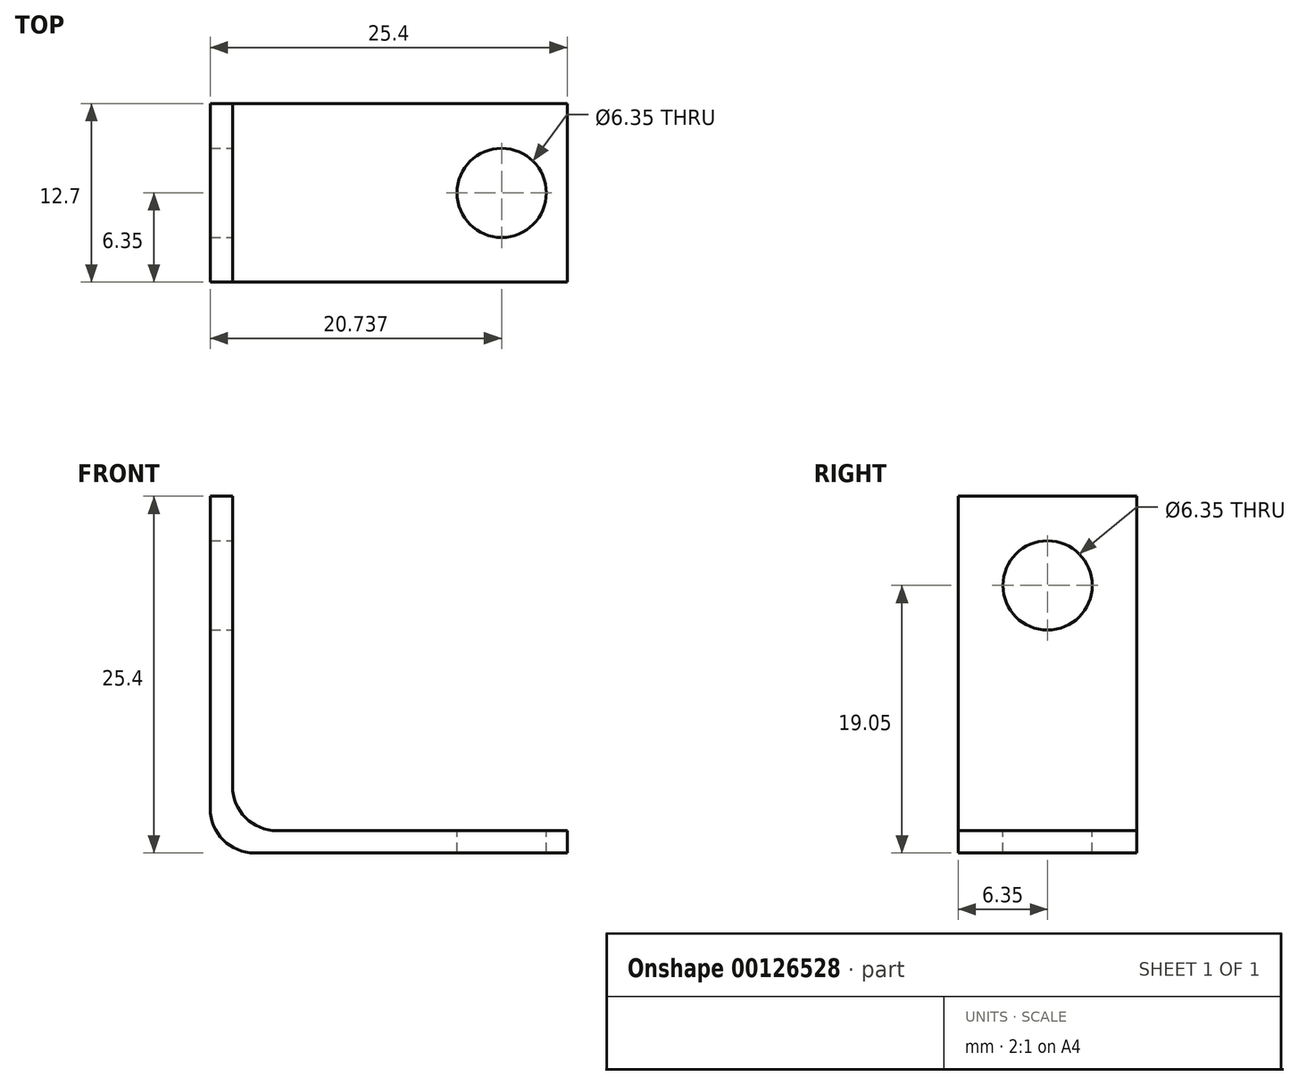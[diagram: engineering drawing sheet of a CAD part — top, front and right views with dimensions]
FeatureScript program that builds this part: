
annotation { "Feature Type Name" : "Feature", "Feature Type Description" : "" }
export const myFeature = defineFeature(function(context is Context, id is Id, definition is map)
    precondition{}
    {
        {
            var Q0;
            Q0=qCreatedBy(makeId("Front.planeOp"),FACE);
            var sketch = newSketch(context, id + "F0", { "sketchPlane" : qUnion([Q0])});
            skLineSegment(sketch, "E0", {"start": v(0, 25.4) * mm, "end": v(1.59, 25.4) * mm});
            skLineSegment(sketch, "E1", {"start": v(1.59, 25.4) * mm, "end": v(1.59, 4.76) * mm});
            skLineSegment(sketch, "E2", {"start": v(25.4, 0) * mm, "end": v(25.4, 1.59) * mm});
            skLineSegment(sketch, "E3", {"start": v(25.4, 1.59) * mm, "end": v(4.76, 1.59) * mm});
            skPoint(sketch, "E4.newPointA", {"position": v(1.59, 0) * mm});
            skPoint(sketch, "E4.newPointB", {"position": v(0, 1.59) * mm});
            skArc(sketch, "E4.filletArc", {"start": v(1.59, 4.76) * mm, "mid": v(2.52, 2.52) * mm, "end": v(4.76, 1.59) * mm});
            skLineSegment(sketch, "E5", {"start": v(0, 25.4) * mm, "end": v(0, 3.18) * mm});
            skLineSegment(sketch, "E6", {"start": v(3.18, 0) * mm, "end": v(25.4, 0) * mm});
            skPoint(sketch, "E7.visualSharp", {"position": v(0, 0) * mm});
            skArc(sketch, "E7.filletArc", {"start": v(0, 3.18) * mm, "mid": v(0.93, 0.93) * mm, "end": v(3.18, 0) * mm});
            skSolve(sketch);
        }
        {
            var Q0;
            Q0 = qSketchRegion(id + "F0", true);
            extrude(context, id + "F1", {"entities" : qUnion([Q0]), "depth" : 12.7 * mm});
        }
        {
            var Q0;
            Q0=qCreatedBy(makeId("Right.planeOp"),FACE);
            cPlane(context, id + "F2", {"entities" : qUnion([Q0]), "cplaneType" : CPlaneType.OFFSET, "offset" : 1.59 * mm, "width" : 152.4 * mm, "height" : 152.4 * mm});
        }
        {
            var Q0;
            Q0=qCreatedBy(id+"F2.planeOp",FACE);
            var sketch = newSketch(context, id + "F3", { "sketchPlane" : qUnion([Q0])});
            skCircle(sketch, "E8", {"center": v(-6.35, 19.05) * mm, "radius": 3.18 * mm});
            skSolve(sketch);
        }
        {
            var Q0;
            Q0=makeQuery(id+"F3.imprint","IMPRINT",FACE,{"disambiguationData":[TD([[makeQuery(id+"F3.imprint","IMPRINT",EDGE,{"derivedFrom":sQuery(id+"F3.wireOp",EDGE,"E8")}),1.0]])]});
            extrude(context, id + "F4", {"entities" : qUnion([Q0]), "operationType" : NewBodyOperationType.REMOVE, "oppositeDirection" : true, "depth" : 1.59 * mm});
        }
        {
            var Q0;
            Q0=qCreatedBy(makeId("Top.planeOp"),FACE);
            cPlane(context, id + "F5", {"entities" : qUnion([Q0]), "cplaneType" : CPlaneType.OFFSET, "offset" : 1.59 * mm, "width" : 152.4 * mm, "height" : 152.4 * mm});
        }
        {
            var Q0;
            Q0=qCreatedBy(id+"F5.planeOp",FACE);
            var sketch = newSketch(context, id + "F6", { "sketchPlane" : qUnion([Q0])});
            skLineSegment(sketch, "E9", {"start": v(1.69, 0) * mm, "end": v(1.69, -6.35) * mm});
            skLineSegment(sketch, "E10", {"start": v(1.69, -6.35) * mm, "end": v(20.74, -6.35) * mm});
            skCircle(sketch, "E11", {"center": v(20.74, -6.35) * mm, "radius": 3.18 * mm});
            skSolve(sketch);
        }
        {
            var Q0;
            Q0=makeQuery(id+"F6.imprint","IMPRINT",FACE,{"disambiguationData":[TD([[makeQuery(id+"F6.imprint","IMPRINT",EDGE,{"derivedFrom":sQuery(id+"F6.wireOp",EDGE,"E11")}),1.0]])]});
            extrude(context, id + "F7", {"entities" : qUnion([Q0]), "operationType" : NewBodyOperationType.REMOVE, "oppositeDirection" : true, "depth" : 1.59 * mm});
        }
    });
